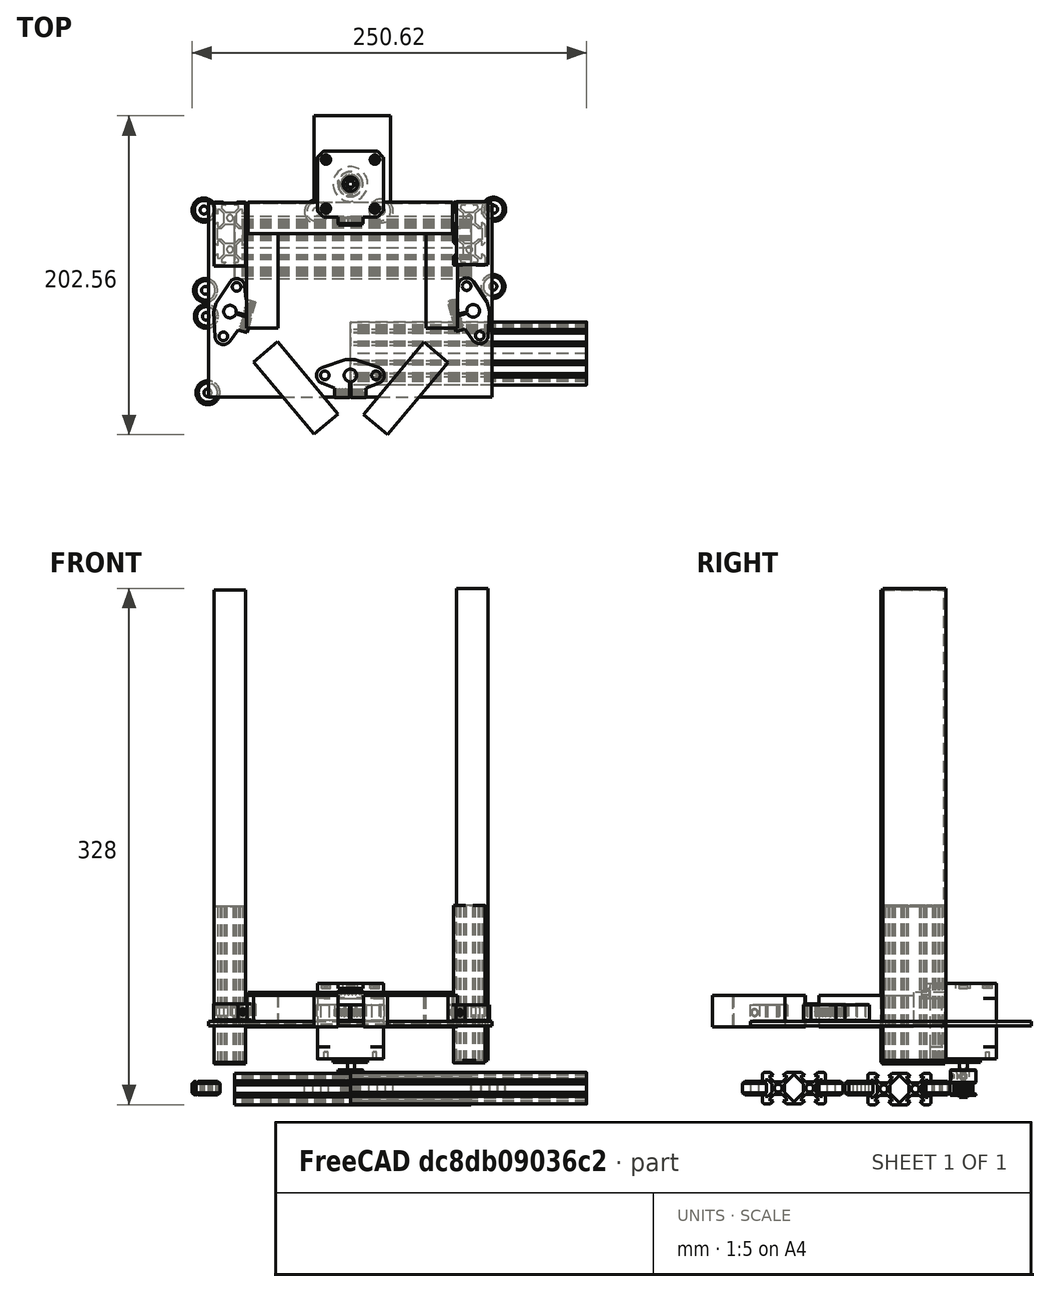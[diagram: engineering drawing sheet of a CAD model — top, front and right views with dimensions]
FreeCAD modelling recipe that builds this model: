
FCSTD DOCUMENT  (FreeCAD 1.0R38641 +468 (Git))
Label: FRAME-ASSEMBLED
License: All rights reserved
LicenseURL: https://en.wikipedia.org/wiki/All_rights_reserved
objects: Part::Feature×17, Sketcher::SketchObject×14, PartDesign::Body×14, PartDesign::Pad×13, Mesh::Feature×6, App::Part×4
note: 98 computed .brp shape members not serialized (recipe doc carries the construction recipe); baked Part::Feature solids carry a one-line shape summary decoded from their .brp

FEATURE [Mesh::Feature] Frame_Plate_Side_Left_1_1_2  label="Frame_Plate_Side_Left_1.1.2"
  Placement = pos=(-61.7,38.5,23.4) rot=(0,1,0;3.14159rad)
FEATURE [Mesh::Feature] Frame_Plate_Side_Right_1_1_2  label="Frame_Plate_Side_Right_1.1.2"
  Placement = pos=(62.7,26.6,23.9) rot=(0,1,0;3.14159rad)
FEATURE [Mesh::Feature] Frame_Plate_TipConnector_1_0_1  label="Frame_Plate_TipConnector_1.0.1"
  Placement = pos=(2e-15,0,0) rot=(0,0.707107,0.707107;3.14159rad)
FEATURE [Sketcher::SketchObject] Sketch
  ArcFitTolerance = 1e-06
  AttachmentSupport = -> [YZ_Plane]
  FullyConstrained = true
  MakeInternals = false
  MapMode = 5
  Placement = pos=(0,0,0) rot=(0.57735,0.57735,0.57735;2.0944rad)
  sketch-geometry (5):
    g0: LineSegment StartX=-10 StartY=10 StartZ=0 EndX=-10 EndY=-10 EndZ=0
    g1: LineSegment StartX=-10 StartY=-10 StartZ=0 EndX=10 EndY=-10 EndZ=0
    g2: LineSegment StartX=10 StartY=-10 StartZ=0 EndX=10 EndY=10 EndZ=0
    g3: LineSegment StartX=10 StartY=10 StartZ=0 EndX=-10 EndY=10 EndZ=0
    g4: GeomPoint [constr] X=0 Y=0 Z=0
  constraints (12):
    c: Coincident(g0,g1)
    c: Coincident(g1,g2)
    c: Coincident(g2,g3)
    c: Coincident(g3,g0)
    c: Vertical(g0)
    c: Vertical(g2)
    c: Horizontal(g1)
    c: Horizontal(g3)
    c: Symmetric(g2,g0,g4)
    c: Coincident(g4,g-1)
    c: DistanceY(g1,g2) = 20
    c: DistanceX(g0,g2) = 20
FEATURE [PartDesign::Pad] Pad
  Direction = (1,0,0)
  Length = 60
  Length2 = 10
  Midplane = true
  Placement = pos=(0,0,0) rot=(1,1,1;2.0944rad)
  Profile = -> Sketch
  ReferenceAxis = -> Sketch [N_Axis]
  Refine = true
  Suppressed = false
  Type = 0
FEATURE [PartDesign::Body] Body  label="2020X60"
  AllowCompound = false
  Group = -> [Pad]
  Origin = -> Origin
  Placement = pos=(35.1549,-8.32071,9.4) rot=(0,0,1;0.872665rad)
  Tip = -> Pad
FEATURE [Sketcher::SketchObject] Sketch001
  ArcFitTolerance = 1e-06
  AttachmentSupport = -> [YZ_Plane001]
  FullyConstrained = true
  MakeInternals = false
  MapMode = 5
  Placement = pos=(0,0,0) rot=(0.57735,0.57735,0.57735;2.0944rad)
  sketch-geometry (5):
    g0: LineSegment StartX=-10 StartY=10 StartZ=0 EndX=-10 EndY=-10 EndZ=0
    g1: LineSegment StartX=-10 StartY=-10 StartZ=0 EndX=10 EndY=-10 EndZ=0
    g2: LineSegment StartX=10 StartY=-10 StartZ=0 EndX=10 EndY=10 EndZ=0
    g3: LineSegment StartX=10 StartY=10 StartZ=0 EndX=-10 EndY=10 EndZ=0
    g4: GeomPoint [constr] X=0 Y=0 Z=0
  constraints (12):
    c: Coincident(g0,g1)
    c: Coincident(g1,g2)
    c: Coincident(g2,g3)
    c: Coincident(g3,g0)
    c: Vertical(g0)
    c: Vertical(g2)
    c: Horizontal(g1)
    c: Horizontal(g3)
    c: Symmetric(g2,g0,g4)
    c: Coincident(g4,g-1)
    c: DistanceY(g1,g2) = 20
    c: DistanceX(g0,g2) = 20
FEATURE [PartDesign::Pad] Pad001
  Direction = (1,0,0)
  Length = 130
  Length2 = 10
  Midplane = true
  Placement = pos=(0,0,0) rot=(1,1,1;2.0944rad)
  Profile = -> Sketch001
  ReferenceAxis = -> Sketch001 [N_Axis]
  Refine = true
  Suppressed = false
  Type = 0
FEATURE [PartDesign::Body] Body001  label="2020X130"
  AllowCompound = false
  Group = -> [Sketch,Pad001,Sketch001]
  Origin = -> Origin001
  Placement = pos=(0,100,11.4) rot=(1,0,0;3.14159rad)
  Tip = -> Pad001
FEATURE [Sketcher::SketchObject] Sketch002
  ArcFitTolerance = 1e-06
  AttachmentSupport = -> [YZ_Plane002]
  FullyConstrained = true
  MakeInternals = false
  MapMode = 5
  Placement = pos=(0,0,0) rot=(0.57735,0.57735,0.57735;2.0944rad)
  sketch-geometry (5):
    g0: LineSegment StartX=-10 StartY=10 StartZ=0 EndX=-10 EndY=-10 EndZ=0
    g1: LineSegment StartX=-10 StartY=-10 StartZ=0 EndX=10 EndY=-10 EndZ=0
    g2: LineSegment StartX=10 StartY=-10 StartZ=0 EndX=10 EndY=10 EndZ=0
    g3: LineSegment StartX=10 StartY=10 StartZ=0 EndX=-10 EndY=10 EndZ=0
    g4: GeomPoint [constr] X=0 Y=0 Z=0
  constraints (12):
    c: Coincident(g0,g1)
    c: Coincident(g1,g2)
    c: Coincident(g2,g3)
    c: Coincident(g3,g0)
    c: Vertical(g0)
    c: Vertical(g2)
    c: Horizontal(g1)
    c: Horizontal(g3)
    c: Symmetric(g2,g0,g4)
    c: Coincident(g4,g-1)
    c: DistanceY(g1,g2) = 20
    c: DistanceX(g0,g2) = 20
FEATURE [PartDesign::Pad] Pad002
  Direction = (1,0,0)
  Length = 60
  Length2 = 10
  Midplane = true
  Placement = pos=(0,0,0) rot=(1,1,1;2.0944rad)
  Profile = -> Sketch002
  ReferenceAxis = -> Sketch002 [N_Axis]
  Refine = true
  Suppressed = false
  Type = 0
FEATURE [PartDesign::Body] Body002  label="2020X60-2"
  AllowCompound = false
  Group = -> [Pad002]
  Origin = -> Origin002
  Placement = pos=(-34.6925,-7.99309,9.4) rot=(0,0,-1;4.01426rad)
  Tip = -> Pad002
FEATURE [Sketcher::SketchObject] Sketch003
  ArcFitTolerance = 1e-06
  AttachmentSupport = -> [YZ_Plane003]
  FullyConstrained = true
  MakeInternals = false
  MapMode = 5
  Placement = pos=(0,0,0) rot=(0.57735,0.57735,0.57735;2.0944rad)
  sketch-geometry (5):
    g0: LineSegment StartX=-10 StartY=10 StartZ=0 EndX=-10 EndY=-10 EndZ=0
    g1: LineSegment StartX=-10 StartY=-10 StartZ=0 EndX=10 EndY=-10 EndZ=0
    g2: LineSegment StartX=10 StartY=-10 StartZ=0 EndX=10 EndY=10 EndZ=0
    g3: LineSegment StartX=10 StartY=10 StartZ=0 EndX=-10 EndY=10 EndZ=0
    g4: GeomPoint [constr] X=0 Y=0 Z=0
  constraints (12):
    c: Coincident(g0,g1)
    c: Coincident(g1,g2)
    c: Coincident(g2,g3)
    c: Coincident(g3,g0)
    c: Vertical(g0)
    c: Vertical(g2)
    c: Horizontal(g1)
    c: Horizontal(g3)
    c: Symmetric(g2,g0,g4)
    c: Coincident(g4,g-1)
    c: DistanceY(g1,g2) = 20
    c: DistanceX(g0,g2) = 20
FEATURE [PartDesign::Pad] Pad003
  Direction = (1,0,0)
  Length = 60
  Length2 = 10
  Midplane = true
  Placement = pos=(0,0,0) rot=(1,1,1;2.0944rad)
  Profile = -> Sketch003
  ReferenceAxis = -> Sketch003 [N_Axis]
  Refine = true
  Suppressed = false
  Type = 0
FEATURE [PartDesign::Body] Body003  label="2020X60-003"
  AllowCompound = false
  Group = -> [Pad003]
  Origin = -> Origin003
  Placement = pos=(-56,60,9.4) rot=(0,0,1;1.5708rad)
  Tip = -> Pad003
FEATURE [Sketcher::SketchObject] Sketch004
  ArcFitTolerance = 1e-06
  AttachmentSupport = -> [YZ_Plane004]
  FullyConstrained = true
  MakeInternals = false
  MapMode = 5
  Placement = pos=(0,0,0) rot=(0.57735,0.57735,0.57735;2.0944rad)
  sketch-geometry (5):
    g0: LineSegment StartX=-10 StartY=10 StartZ=0 EndX=-10 EndY=-10 EndZ=0
    g1: LineSegment StartX=-10 StartY=-10 StartZ=0 EndX=10 EndY=-10 EndZ=0
    g2: LineSegment StartX=10 StartY=-10 StartZ=0 EndX=10 EndY=10 EndZ=0
    g3: LineSegment StartX=10 StartY=10 StartZ=0 EndX=-10 EndY=10 EndZ=0
    g4: GeomPoint [constr] X=0 Y=0 Z=0
  constraints (12):
    c: Coincident(g0,g1)
    c: Coincident(g1,g2)
    c: Coincident(g2,g3)
    c: Coincident(g3,g0)
    c: Vertical(g0)
    c: Vertical(g2)
    c: Horizontal(g1)
    c: Horizontal(g3)
    c: Symmetric(g2,g0,g4)
    c: Coincident(g4,g-1)
    c: DistanceY(g1,g2) = 20
    c: DistanceX(g0,g2) = 20
FEATURE [PartDesign::Pad] Pad004
  Direction = (1,0,0)
  Length = 60
  Length2 = 10
  Midplane = true
  Placement = pos=(0,0,0) rot=(1,1,1;2.0944rad)
  Profile = -> Sketch004
  ReferenceAxis = -> Sketch004 [N_Axis]
  Refine = true
  Suppressed = false
  Type = 0
FEATURE [PartDesign::Body] Body004  label="2020X60-004"
  AllowCompound = false
  Group = -> [Pad004]
  Origin = -> Origin004
  Placement = pos=(58,60,9.4) rot=(0,0,1;1.5708rad)
  Tip = -> Pad004
FEATURE [App::Part] Part  label="BOTTOM PLATE"
  Group = -> [Body004,Body003,Body001,Body,Frame_Plate_TipConnector_1_0_1,Frame_Plate_Side_Right_1_1_2,Frame_Plate_Side_Left_1_1_2,Body002]
  Origin = -> Origin005
  Placement = pos=(0,0,0) rot=(0,1,0;3.14159rad)
FEATURE [Mesh::Feature] Frame_Plate_Side_Left_1_1_003  label="Frame_Plate_Side_Left_1.1.003"
  Placement = pos=(-61.7,38.5,23.4) rot=(0,1,0;3.14159rad)
FEATURE [Mesh::Feature] Frame_Plate_Side_Right_1_1_003  label="Frame_Plate_Side_Right_1.1.003"
  Placement = pos=(62.7,26.6,23.9) rot=(0,1,0;3.14159rad)
FEATURE [Mesh::Feature] Frame_Plate_TipConnector_1_0_002  label="Frame_Plate_TipConnector_1.0.002"
  Placement = pos=(2e-15,0,0) rot=(0,0.707107,0.707107;3.14159rad)
FEATURE [Sketcher::SketchObject] Sketch005
  ArcFitTolerance = 1e-06
  AttachmentSupport = -> [YZ_Plane006]
  FullyConstrained = true
  MakeInternals = false
  MapMode = 5
  Placement = pos=(0,0,0) rot=(0.57735,0.57735,0.57735;2.0944rad)
  sketch-geometry (5):
    g0: LineSegment StartX=-10 StartY=10 StartZ=0 EndX=-10 EndY=-10 EndZ=0
    g1: LineSegment StartX=-10 StartY=-10 StartZ=0 EndX=10 EndY=-10 EndZ=0
    g2: LineSegment StartX=10 StartY=-10 StartZ=0 EndX=10 EndY=10 EndZ=0
    g3: LineSegment StartX=10 StartY=10 StartZ=0 EndX=-10 EndY=10 EndZ=0
    g4: GeomPoint [constr] X=0 Y=0 Z=0
  constraints (12):
    c: Coincident(g0,g1)
    c: Coincident(g1,g2)
    c: Coincident(g2,g3)
    c: Coincident(g3,g0)
    c: Vertical(g0)
    c: Vertical(g2)
    c: Horizontal(g1)
    c: Horizontal(g3)
    c: Symmetric(g2,g0,g4)
    c: Coincident(g4,g-1)
    c: DistanceY(g1,g2) = 20
    c: DistanceX(g0,g2) = 20
FEATURE [PartDesign::Pad] Pad005
  Direction = (1,0,0)
  Length = 60
  Length2 = 10
  Midplane = true
  Placement = pos=(0,0,0) rot=(1,1,1;2.0944rad)
  Profile = -> Sketch005
  ReferenceAxis = -> Sketch005 [N_Axis]
  Refine = true
  Suppressed = false
  Type = 0
FEATURE [PartDesign::Body] Body005  label="2020X131"
  AllowCompound = false
  Group = -> [Pad005]
  Origin = -> Origin006
  Placement = pos=(35.1549,-8.32071,9.4) rot=(0,0,1;0.872665rad)
  Tip = -> Pad005
FEATURE [Sketcher::SketchObject] Sketch006
  ArcFitTolerance = 1e-06
  AttachmentSupport = -> [YZ_Plane007]
  FullyConstrained = true
  MakeInternals = false
  MapMode = 5
  Placement = pos=(0,0,0) rot=(0.57735,0.57735,0.57735;2.0944rad)
  sketch-geometry (5):
    g0: LineSegment StartX=-10 StartY=10 StartZ=0 EndX=-10 EndY=-10 EndZ=0
    g1: LineSegment StartX=-10 StartY=-10 StartZ=0 EndX=10 EndY=-10 EndZ=0
    g2: LineSegment StartX=10 StartY=-10 StartZ=0 EndX=10 EndY=10 EndZ=0
    g3: LineSegment StartX=10 StartY=10 StartZ=0 EndX=-10 EndY=10 EndZ=0
    g4: GeomPoint [constr] X=0 Y=0 Z=0
  constraints (12):
    c: Coincident(g0,g1)
    c: Coincident(g1,g2)
    c: Coincident(g2,g3)
    c: Coincident(g3,g0)
    c: Vertical(g0)
    c: Vertical(g2)
    c: Horizontal(g1)
    c: Horizontal(g3)
    c: Symmetric(g2,g0,g4)
    c: Coincident(g4,g-1)
    c: DistanceY(g1,g2) = 20
    c: DistanceX(g0,g2) = 20
FEATURE [PartDesign::Pad] Pad006
  Direction = (1,0,0)
  Length = 130
  Length2 = 10
  Midplane = true
  Placement = pos=(0,0,0) rot=(1,1,1;2.0944rad)
  Profile = -> Sketch006
  ReferenceAxis = -> Sketch006 [N_Axis]
  Refine = true
  Suppressed = false
  Type = 0
FEATURE [PartDesign::Body] Body006  label="2020X132"
  AllowCompound = false
  Group = -> [Sketch005,Pad006,Sketch006]
  Origin = -> Origin007
  Placement = pos=(0,100,11.4) rot=(1,0,0;3.14159rad)
  Tip = -> Pad006
FEATURE [Sketcher::SketchObject] Sketch007
  ArcFitTolerance = 1e-06
  AttachmentSupport = -> [YZ_Plane008]
  FullyConstrained = true
  MakeInternals = false
  MapMode = 5
  Placement = pos=(0,0,0) rot=(0.57735,0.57735,0.57735;2.0944rad)
  sketch-geometry (5):
    g0: LineSegment StartX=-10 StartY=10 StartZ=0 EndX=-10 EndY=-10 EndZ=0
    g1: LineSegment StartX=-10 StartY=-10 StartZ=0 EndX=10 EndY=-10 EndZ=0
    g2: LineSegment StartX=10 StartY=-10 StartZ=0 EndX=10 EndY=10 EndZ=0
    g3: LineSegment StartX=10 StartY=10 StartZ=0 EndX=-10 EndY=10 EndZ=0
    g4: GeomPoint [constr] X=0 Y=0 Z=0
  constraints (12):
    c: Coincident(g0,g1)
    c: Coincident(g1,g2)
    c: Coincident(g2,g3)
    c: Coincident(g3,g0)
    c: Vertical(g0)
    c: Vertical(g2)
    c: Horizontal(g1)
    c: Horizontal(g3)
    c: Symmetric(g2,g0,g4)
    c: Coincident(g4,g-1)
    c: DistanceY(g1,g2) = 20
    c: DistanceX(g0,g2) = 20
FEATURE [PartDesign::Pad] Pad007
  Direction = (1,0,0)
  Length = 60
  Length2 = 10
  Midplane = true
  Placement = pos=(0,0,0) rot=(1,1,1;2.0944rad)
  Profile = -> Sketch007
  ReferenceAxis = -> Sketch007 [N_Axis]
  Refine = true
  Suppressed = false
  Type = 0
FEATURE [PartDesign::Body] Body007  label="2020X60-005"
  AllowCompound = false
  Group = -> [Pad007]
  Origin = -> Origin008
  Placement = pos=(-34.6925,-7.99309,9.4) rot=(0,0,-1;4.01426rad)
  Tip = -> Pad007
FEATURE [Sketcher::SketchObject] Sketch008
  ArcFitTolerance = 1e-06
  AttachmentSupport = -> [YZ_Plane009]
  FullyConstrained = true
  MakeInternals = false
  MapMode = 5
  Placement = pos=(0,0,0) rot=(0.57735,0.57735,0.57735;2.0944rad)
  sketch-geometry (5):
    g0: LineSegment StartX=-10 StartY=10 StartZ=0 EndX=-10 EndY=-10 EndZ=0
    g1: LineSegment StartX=-10 StartY=-10 StartZ=0 EndX=10 EndY=-10 EndZ=0
    g2: LineSegment StartX=10 StartY=-10 StartZ=0 EndX=10 EndY=10 EndZ=0
    g3: LineSegment StartX=10 StartY=10 StartZ=0 EndX=-10 EndY=10 EndZ=0
    g4: GeomPoint [constr] X=0 Y=0 Z=0
  constraints (12):
    c: Coincident(g0,g1)
    c: Coincident(g1,g2)
    c: Coincident(g2,g3)
    c: Coincident(g3,g0)
    c: Vertical(g0)
    c: Vertical(g2)
    c: Horizontal(g1)
    c: Horizontal(g3)
    c: Symmetric(g2,g0,g4)
    c: Coincident(g4,g-1)
    c: DistanceY(g1,g2) = 20
    c: DistanceX(g0,g2) = 20
FEATURE [PartDesign::Pad] Pad008
  Direction = (1,0,0)
  Length = 60
  Length2 = 10
  Midplane = true
  Placement = pos=(0,0,0) rot=(1,1,1;2.0944rad)
  Profile = -> Sketch008
  ReferenceAxis = -> Sketch008 [N_Axis]
  Refine = true
  Suppressed = false
  Type = 0
FEATURE [PartDesign::Body] Body008  label="2020X60-006"
  AllowCompound = false
  Group = -> [Pad008]
  Origin = -> Origin009
  Placement = pos=(-56,60,9.4) rot=(0,0,1;1.5708rad)
  Tip = -> Pad008
FEATURE [Sketcher::SketchObject] Sketch009
  ArcFitTolerance = 1e-06
  AttachmentSupport = -> [YZ_Plane010]
  FullyConstrained = true
  MakeInternals = false
  MapMode = 5
  Placement = pos=(0,0,0) rot=(0.57735,0.57735,0.57735;2.0944rad)
  sketch-geometry (5):
    g0: LineSegment StartX=-10 StartY=10 StartZ=0 EndX=-10 EndY=-10 EndZ=0
    g1: LineSegment StartX=-10 StartY=-10 StartZ=0 EndX=10 EndY=-10 EndZ=0
    g2: LineSegment StartX=10 StartY=-10 StartZ=0 EndX=10 EndY=10 EndZ=0
    g3: LineSegment StartX=10 StartY=10 StartZ=0 EndX=-10 EndY=10 EndZ=0
    g4: GeomPoint [constr] X=0 Y=0 Z=0
  constraints (12):
    c: Coincident(g0,g1)
    c: Coincident(g1,g2)
    c: Coincident(g2,g3)
    c: Coincident(g3,g0)
    c: Vertical(g0)
    c: Vertical(g2)
    c: Horizontal(g1)
    c: Horizontal(g3)
    c: Symmetric(g2,g0,g4)
    c: Coincident(g4,g-1)
    c: DistanceY(g1,g2) = 20
    c: DistanceX(g0,g2) = 20
FEATURE [PartDesign::Pad] Pad009
  Direction = (1,0,0)
  Length = 60
  Length2 = 10
  Midplane = true
  Placement = pos=(0,0,0) rot=(1,1,1;2.0944rad)
  Profile = -> Sketch009
  ReferenceAxis = -> Sketch009 [N_Axis]
  Refine = true
  Suppressed = false
  Type = 0
FEATURE [PartDesign::Body] Body009  label="2020X60-007"
  AllowCompound = false
  Group = -> [Pad009]
  Origin = -> Origin010
  Placement = pos=(58,60,9.4) rot=(0,0,1;1.5708rad)
  Tip = -> Pad009
FEATURE [App::Part] Part001  label="TOP PLATE001"
  Group = -> [Body009,Body008,Body006,Body005,Frame_Plate_TipConnector_1_0_002,Frame_Plate_Side_Right_1_1_003,Frame_Plate_Side_Left_1_1_003,Body007]
  Origin = -> Origin011
  Placement = pos=(0,0,253.8) rot=(0,0,1;0rad)
FEATURE [Sketcher::SketchObject] Sketch010
  ArcFitTolerance = 1e-06
  AttachmentSupport = -> [XY_Plane013]
  FullyConstrained = true
  MakeInternals = false
  MapMode = 5
  sketch-geometry (5):
    g0: LineSegment StartX=10 StartY=-20 StartZ=0 EndX=10 EndY=20 EndZ=0
    g1: LineSegment StartX=10 StartY=20 StartZ=0 EndX=-10 EndY=20 EndZ=0
    g2: LineSegment StartX=-10 StartY=20 StartZ=0 EndX=-10 EndY=-20 EndZ=0
    g3: LineSegment StartX=-10 StartY=-20 StartZ=0 EndX=10 EndY=-20 EndZ=0
    g4: GeomPoint [constr] X=0 Y=0 Z=0
  constraints (12):
    c: Coincident(g0,g1)
    c: Coincident(g1,g2)
    c: Coincident(g2,g3)
    c: Coincident(g3,g0)
    c: Vertical(g0)
    c: Vertical(g2)
    c: Horizontal(g1)
    c: Horizontal(g3)
    c: Symmetric(g2,g0,g4)
    c: Coincident(g4,g-1)
    c: DistanceX(g1,g0) = 20
    c: DistanceY(g0,g0) = 40
FEATURE [PartDesign::Pad] Pad010
  Direction = (0,0,1)
  Length = 300
  Length2 = 10
  Profile = -> Sketch010
  ReferenceAxis = -> Sketch010 [N_Axis]
  Refine = true
  Suppressed = false
  Type = 0
FEATURE [PartDesign::Body] Body010  label="2040X300"
  AllowCompound = false
  Group = -> [Sketch010,Pad010]
  Origin = -> Origin013
  Placement = pos=(77.3,90.5,-22) rot=(0,0,1;0rad)
  Tip = -> Pad010
FEATURE [Sketcher::SketchObject] Sketch011
  ArcFitTolerance = 1e-06
  AttachmentSupport = -> [XY_Plane014]
  FullyConstrained = true
  MakeInternals = false
  MapMode = 5
  sketch-geometry (5):
    g0: LineSegment StartX=10 StartY=-20 StartZ=0 EndX=10 EndY=20 EndZ=0
    g1: LineSegment StartX=10 StartY=20 StartZ=0 EndX=-10 EndY=20 EndZ=0
    g2: LineSegment StartX=-10 StartY=20 StartZ=0 EndX=-10 EndY=-20 EndZ=0
    g3: LineSegment StartX=-10 StartY=-20 StartZ=0 EndX=10 EndY=-20 EndZ=0
    g4: GeomPoint [constr] X=0 Y=0 Z=0
  constraints (12):
    c: Coincident(g0,g1)
    c: Coincident(g1,g2)
    c: Coincident(g2,g3)
    c: Coincident(g3,g0)
    c: Vertical(g0)
    c: Vertical(g2)
    c: Horizontal(g1)
    c: Horizontal(g3)
    c: Symmetric(g2,g0,g4)
    c: Coincident(g4,g-1)
    c: DistanceX(g1,g0) = 20
    c: DistanceY(g0,g0) = 40
FEATURE [PartDesign::Pad] Pad011
  Direction = (0,0,1)
  Length = 300
  Length2 = 10
  Profile = -> Sketch011
  ReferenceAxis = -> Sketch011 [N_Axis]
  Refine = true
  Suppressed = false
  Type = 0
FEATURE [PartDesign::Body] Body011  label="2040X301"
  AllowCompound = false
  Group = -> [Sketch011,Pad011]
  Origin = -> Origin014
  Placement = pos=(-76.5,89.3,-23.1) rot=(0,0,1;0rad)
  Tip = -> Pad011
FEATURE [App::Part] Part002  label="VERTICAL"
  Group = -> [Body010,Body011]
  Origin = -> Origin012
FEATURE [Part::Feature] Part__Feature  label="Aluminium2040 Vslot Profile by prodes"
  Placement = pos=(-76.5,100,-24) rot=(-0.707107,0.707107,0;3.14159rad)
  shape: bbox 20 x 40 x 100 mm, 110 faces (baked)
FEATURE [Part::Feature] Part__Feature001  label="Aluminium2040 Vslot Profile by prodes001"
  Placement = pos=(75.5,100,-23.5) rot=(0.707107,-0.707107,0;3.14159rad)
  shape: bbox 20 x 40 x 100 mm, 110 faces (baked)
FEATURE [Sketcher::SketchObject] Sketch012
  ArcFitTolerance = 1e-06
  AttachmentSupport = -> [XY_Plane016]
  FullyConstrained = false
  MakeInternals = false
  MapMode = 5
  sketch-geometry (8):
    g0: LineSegment StartX=-90 StartY=109.336 StartZ=0 EndX=-90 EndY=-13.6673 EndZ=0
    g1: LineSegment StartX=-90 StartY=-13.6673 StartZ=0 EndX=90 EndY=-13.6673 EndZ=0
    g2: LineSegment StartX=90 StartY=-13.6673 StartZ=0 EndX=90 EndY=109.336 EndZ=0
    g3: LineSegment StartX=-90 StartY=109.336 StartZ=0 EndX=-22.9635 EndY=109.336 EndZ=0
    g4: LineSegment StartX=-22.9635 StartY=109.336 StartZ=0 EndX=-22.9635 EndY=164.832 EndZ=0
    g5: LineSegment StartX=-22.9635 StartY=164.832 StartZ=0 EndX=25.5 EndY=164.832 EndZ=0
    g6: LineSegment StartX=25.5 StartY=164.832 StartZ=0 EndX=25.5 EndY=109.336 EndZ=0
    g7: LineSegment StartX=25.5 StartY=109.336 StartZ=0 EndX=90 EndY=109.336 EndZ=0
  constraints (18):
    c: Coincident(g0,g1)
    c: Coincident(g1,g2)
    c: Vertical(g0)
    c: Vertical(g2)
    c: Symmetric(g1,g0,g-2)
    c: DistanceX(g0,g1) = 180
    c: Coincident(g3,g0)
    c: Horizontal(g3)
    c: Vertical(g4)
    c: Coincident(g5,g4)
    c: Horizontal(g5)
    c: Coincident(g6,g5)
    c: Vertical(g6)
    c: Coincident(g7,g6)
    c: Coincident(g7,g2)
    c: Horizontal(g7)
    c: Horizontal(g4,g6)
    c: Coincident(g4,g3)
FEATURE [PartDesign::Pad] Pad012
  Direction = (0,0,1)
  Length = 3
  Length2 = 10
  Profile = -> Sketch012
  ReferenceAxis = -> Sketch012 [N_Axis]
  Refine = true
  Suppressed = false
  Type = 0
FEATURE [PartDesign::Body] Body012  label="Body"
  AllowCompound = false
  Group = -> [Sketch012,Pad012]
  Origin = -> Origin016
  Tip = -> Pad012
FEATURE [Part::Feature] Part__Feature002  label="shf8mm"
  Placement = pos=(0,0,3.5) rot=(0,0,1;0rad)
  shape: bbox 43 x 24 x 10 mm, 66 faces (baked)
FEATURE [Part::Feature] Part__Feature003  label="shf8mm001"
  Placement = pos=(78,41,3.5) rot=(0,0,1;4.97419rad)
  shape: bbox 26.55 x 41.89 x 10 mm, 66 faces (baked)
FEATURE [Part::Feature] Part__Feature004  label="shf8mm002"
  Placement = pos=(-76.5,40.5,4) rot=(0,0,1;1.309rad)
  shape: bbox 26.55 x 41.89 x 10 mm, 66 faces (baked)
FEATURE [Part::Feature] Part__Feature005  label="Профиль V-slot 20x40"
  Placement = pos=(8.8e-15,24,-39.5) rot=(0,1,0;1.5708rad)
  shape: bbox 150 x 40 x 20 mm, 80 faces (baked)
FEATURE [Part::Feature] Part__Feature006  label="Профиль V-slot 20x041"
  Placement = pos=(-73.5,91,-40) rot=(0,1,0;1.5708rad)
  shape: bbox 150 x 40 x 20 mm, 80 faces (baked)
FEATURE [Part::Feature] Part__Feature007  label="15mm-wheel v1"
  Placement = pos=(-93,105,-39.5) rot=(1,0,0;1.5708rad)
  shape: bbox 15.23 x 15.23 x 8.8 mm, 6 faces (baked)
FEATURE [Part::Feature] Part__Feature008  label="15mm-wheel v002"
  Placement = pos=(-92,54,-39.5) rot=(1,0,0;1.5708rad)
  shape: bbox 15.23 x 15.23 x 8.8 mm, 6 faces (baked)
FEATURE [Part::Feature] Part__Feature009  label="15mm-wheel v003"
  Placement = pos=(91,105.5,-39.5) rot=(1,0,0;1.5708rad)
  shape: bbox 15.23 x 15.23 x 8.8 mm, 6 faces (baked)
FEATURE [Part::Feature] Part__Feature010  label="15mm-wheel v004"
  Placement = pos=(-91.5,37.5,-39.5) rot=(1,0,0;1.5708rad)
  shape: bbox 15.23 x 15.23 x 8.8 mm, 6 faces (baked)
FEATURE [Part::Feature] Part__Feature011  label="15mm-wheel v005"
  Placement = pos=(-90.5,-11,-39.5) rot=(1,0,0;1.5708rad)
  shape: bbox 15.23 x 15.23 x 8.8 mm, 6 faces (baked)
FEATURE [Part::Feature] Part__Feature012  label="15mm-wheel v006"
  Placement = pos=(90.5,56.5,-39.5) rot=(1,0,0;1.5708rad)
  shape: bbox 15.23 x 15.23 x 8.8 mm, 6 faces (baked)
FEATURE [Part::Feature] Part__Feature013  label="15mm-wheel v007"
  Placement = pos=(-21.5,104,-39.5) rot=(1,0,0;1.5708rad)
  shape: bbox 15.23 x 15.23 x 8.8 mm, 6 faces (baked)
FEATURE [Part::Feature] Part__Feature014  label="15mm-wheel v008"
  Placement = pos=(19.5,104.5,-39.5) rot=(1,0,0;1.5708rad)
  shape: bbox 15.23 x 15.23 x 8.8 mm, 6 faces (baked)
FEATURE [Part::Feature] Part__Feature015  label="NEMA17 42-40 v3"
  Placement = pos=(0,121.5,-21) rot=(1,0,0;1.5708rad)
  shape: bbox 42.02 x 47.1 x 72.37 mm, 266 faces (baked)
FEATURE [Part::Feature] Part__Feature016  label="GT2_20T_8_6"
  Placement = pos=(-3e-16,121.5,-28) rot=(0,1,0;3.14159rad)
  shape: bbox 17.32 x 17.32 x 16 mm, 247 faces (baked)
FEATURE [Sketcher::SketchObject] Sketch013
  ArcFitTolerance = 1e-06
  AttachmentSupport = -> [XY_Plane017]
  FullyConstrained = false
  MakeInternals = false
  MapMode = 5
  sketch-geometry (7):
    g0: ArcOfCircle CenterX=0 CenterY=120.624 CenterZ=0 NormalX=0 NormalY=0 NormalZ=1 AngleXU=0 Radius=8.68684 StartAngle=0.46069 EndAngle=2.82489
    g1: ArcOfCircle CenterX=19.5701 CenterY=104.364 CenterZ=0 NormalX=0 NormalY=0 NormalZ=1 AngleXU=0 Radius=7.72644 StartAngle=3.11528 EndAngle=4.71239
    g2: ArcOfCircle CenterX=-21.2845 CenterY=103.754 CenterZ=0 NormalX=0 NormalY=0 NormalZ=1 AngleXU=0 Radius=7.32007 StartAngle=4.71239 EndAngle=6.31096
    g3: LineSegment StartX=7.78121 StartY=124.486 StartZ=0 EndX=11.8463 EndY=104.567 EndZ=0
    g4: LineSegment StartX=-8.25482 StartY=123.33 StartZ=0 EndX=-13.9673 EndY=103.957 EndZ=0
    g5: LineSegment StartX=19.5701 StartY=96.6374 StartZ=0 EndX=94.3687 EndY=96.6374 EndZ=0
    g6: LineSegment StartX=-21.2845 StartY=96.434 StartZ=0 EndX=-85.6016 EndY=96.434 EndZ=0
  constraints (9):
    c: PointOnObject(g0,g-2)
    c: Coincident(g3,g0)
    c: Coincident(g3,g1)
    c: Coincident(g4,g0)
    c: Coincident(g4,g2)
    c: Coincident(g5,g1)
    c: Horizontal(g5)
    c: Coincident(g6,g2)
    c: Horizontal(g6)
FEATURE [PartDesign::Body] Body013  label="correa abierta"
  AllowCompound = false
  Group = -> [Sketch013]
  Origin = -> Origin017
  Placement = pos=(0,0,-10.5) rot=(0,0,1;0rad)
FEATURE [App::Part] Part003  label="YAXIS RAIL"
  Group = -> [Body012,Part__Feature002,Part__Feature004,Part__Feature003,Body013]
  Origin = -> Origin015
  Placement = pos=(0,0,-28.5) rot=(0,0,1;0rad)
